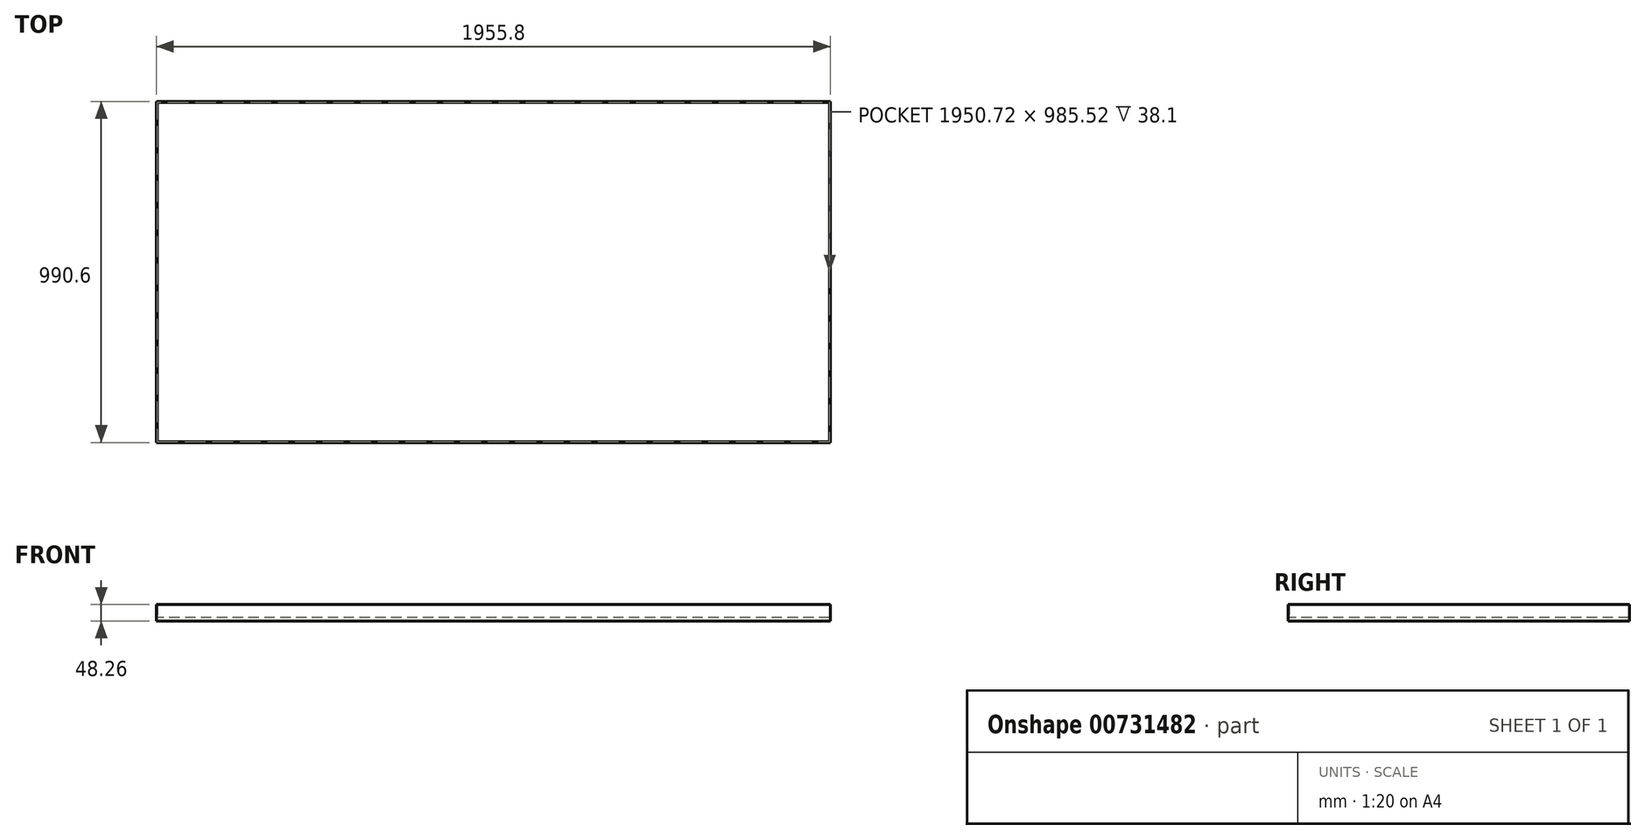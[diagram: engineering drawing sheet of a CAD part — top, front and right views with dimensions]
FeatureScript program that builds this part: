
annotation { "Feature Type Name" : "Feature", "Feature Type Description" : "" }
export const myFeature = defineFeature(function(context is Context, id is Id, definition is map)
    precondition{}
    {
        {
            var Q0;
            Q0=qCreatedBy(makeId("Top.planeOp"),FACE);
            var sketch = newSketch(context, id + "F0", { "sketchPlane" : qUnion([Q0])});
            skLineSegment(sketch, "E0.bottom", {"start": v(0, 0) * mm, "end": v(1955.8, 0) * mm});
            skLineSegment(sketch, "E0.top", {"start": v(0, 990.6) * mm, "end": v(1955.8, 990.6) * mm});
            skLineSegment(sketch, "E0.left", {"start": v(0, 0) * mm, "end": v(0, 990.6) * mm});
            skLineSegment(sketch, "E0.right", {"start": v(1955.8, 0) * mm, "end": v(1955.8, 990.6) * mm});
            skSolve(sketch);
        }
        {
            var Q0;
            Q0=makeQuery(id+"F0.imprint","IMPRINT",FACE,{"disambiguationData":[TD([[makeQuery(id+"F0.imprint","IMPRINT",EDGE,{"derivedFrom":sQuery(id+"F0.wireOp",EDGE,"E0.bottom")}),1.0]])]});
            extrude(context, id + "F1", {"entities" : qUnion([Q0]), "depth" : 10.16 * mm, "offsetDistance" : 25.4 * mm});
        }
        {
            var Q0;
            Q0=makeQuery(id+"F1.opExtrude","CAP_FACE",FACE,{"disambiguationData":[OSD([sQuery(id+"F0.wireOp",EDGE,"E0.bottom"),sQuery(id+"F0.wireOp",EDGE,"E0.top"),sQuery(id+"F0.wireOp",EDGE,"E0.left"),sQuery(id+"F0.wireOp",EDGE,"E0.right")])],"isStart":false});
            var sketch = newSketch(context, id + "F2", { "sketchPlane" : qUnion([Q0])});
            skLineSegment(sketch, "E1", {"start": v(0, 125.16) * mm, "end": v(2.54, 125.16) * mm});
            skLineSegment(sketch, "E2", {"start": v(9.51, 0) * mm, "end": v(9.51, 2.54) * mm});
            skLineSegment(sketch, "E3", {"start": v(1955.8, 977.44) * mm, "end": v(1953.26, 977.44) * mm});
            skLineSegment(sketch, "E4", {"start": v(1948.8, 990.6) * mm, "end": v(1948.8, 988.06) * mm});
            skLineSegment(sketch, "E5.bottom", {"start": v(1953.26, 988.06) * mm, "end": v(2.54, 988.06) * mm});
            skLineSegment(sketch, "E5.top", {"start": v(1953.26, 2.54) * mm, "end": v(2.54, 2.54) * mm});
            skLineSegment(sketch, "E5.left", {"start": v(1953.26, 988.06) * mm, "end": v(1953.26, 2.54) * mm});
            skLineSegment(sketch, "E5.right", {"start": v(2.54, 988.06) * mm, "end": v(2.54, 2.54) * mm});
            skSolve(sketch);
        }
        {
            var Q0;
            {var subQ4=sQuery(id+"F2.wireOp",EDGE,"E1");Q0=makeQuery(id+"F2.imprint","IMPRINT",FACE,{"disambiguationData":[TD([[makeQuery(id+"F2.imprint","IMPRINT",EDGE,{"derivedFrom":subQ4}),-1.0]])]});}
            var Q1;
            {var subQ5=sQuery(id+"F2.wireOp",EDGE,"E1");Q1=makeQuery(id+"F2.imprint","IMPRINT",FACE,{"disambiguationData":[TD([[makeQuery(id+"F2.imprint","IMPRINT",EDGE,{"derivedFrom":subQ5}),1.0]])]});}
            var Q2;
            {var subQ7=sQuery(id+"F2.wireOp",EDGE,"E3");Q2=makeQuery(id+"F2.imprint","IMPRINT",FACE,{"disambiguationData":[TD([[makeQuery(id+"F2.imprint","IMPRINT",EDGE,{"derivedFrom":subQ7}),-1.0]])]});}
            var Q3;
            {var subQ7=sQuery(id+"F2.wireOp",EDGE,"E2");Q3=makeQuery(id+"F2.imprint","IMPRINT",FACE,{"disambiguationData":[TD([[makeQuery(id+"F2.imprint","IMPRINT",EDGE,{"derivedFrom":subQ7}),-1.0]])]});}
            extrude(context, id + "F3", {"entities" : qUnion([Q0, Q1, Q2, Q3]), "operationType" : NewBodyOperationType.ADD, "depth" : 38.1 * mm, "offsetDistance" : 25.4 * mm});
        }
    });
